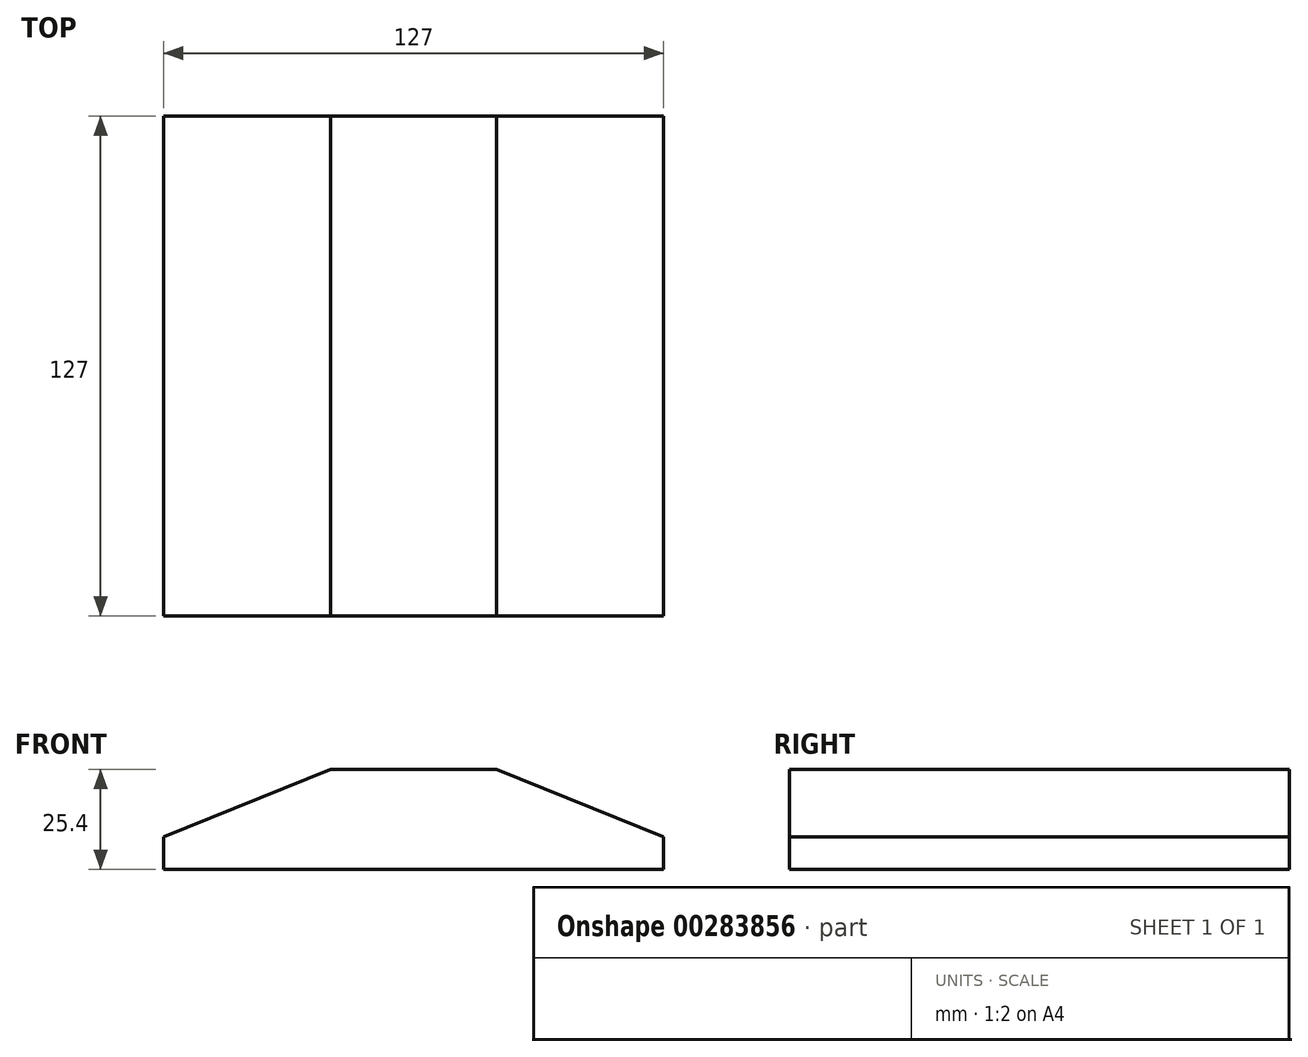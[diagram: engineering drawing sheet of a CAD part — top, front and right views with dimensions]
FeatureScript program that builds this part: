
annotation { "Feature Type Name" : "Feature", "Feature Type Description" : "" }
export const myFeature = defineFeature(function(context is Context, id is Id, definition is map)
    precondition{}
    {
        {
            var Q0;
            Q0=qCreatedBy(makeId("Front.planeOp"),FACE);
            var sketch = newSketch(context, id + "F0", { "sketchPlane" : qUnion([Q0])});
            skLineSegment(sketch, "E0.bottom", {"start": v(-63.5, -12.7) * mm, "end": v(63.5, -12.7) * mm});
            skLineSegment(sketch, "E0.top", {"start": v(-21.1, 12.7) * mm, "end": v(21.1, 12.7) * mm});
            skLineSegment(sketch, "E0.left", {"start": v(-63.5, -12.7) * mm, "end": v(-63.5, -4.43) * mm});
            skLineSegment(sketch, "E0.right", {"start": v(63.5, -12.7) * mm, "end": v(63.5, -4.43) * mm});
            skPoint(sketch, "E0.middle", {"position": v(0, 0) * mm});
            skLineSegment(sketch, "E1", {"start": v(21.1, 12.7) * mm, "end": v(63.5, -4.43) * mm});
            skPoint(sketch, "E2.orphan", {"position": v(63.5, 12.7) * mm});
            skLineSegment(sketch, "E3", {"start": v(0, 27.06) * mm, "end": v(0, -66.33) * mm, "construction": true});
            skLineSegment(sketch, "E4", {"start": v(-63.5, -4.43) * mm, "end": v(-21.1, 12.7) * mm});
            skPoint(sketch, "E5.orphan", {"position": v(-63.5, 12.7) * mm});
            skSolve(sketch);
        }
        {
            var Q0;
            Q0=makeQuery(id+"F0.imprint","IMPRINT",FACE,{"disambiguationData":[TD([[makeQuery(id+"F0.imprint","IMPRINT",EDGE,{"derivedFrom":sQuery(id+"F0.wireOp",EDGE,"E0.bottom")}),1.0]])]});
            extrude(context, id + "F1", {"entities" : qUnion([Q0]), "endBound" : BoundingType.SYMMETRIC, "depth" : 127 * mm});
        }
    });
